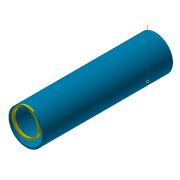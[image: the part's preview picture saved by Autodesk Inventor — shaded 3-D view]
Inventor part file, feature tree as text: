
AUTODESK INVENTOR PART (.ipt)
format: ipt  version: 2016 (Build 200138000, 138)  size: 161,792 bytes
history: native  units: in
note: dims shown in document units (in); Inventor stores cm internally (conversion verified against a paired STEP export)
features: sketch x8, extrude x4, plane x3, other x2, hole x1
ambient origin geometry x8: Origin, YZ Plane, XZ Plane, XY Plane, X Axis, Y Axis, Z Axis, Center Point
bodies: Solid1 (feature_tree)
feature tree (18):
  extrude  "Extrusion1"  Depth=0.1535in
  sketch  "Sketch2"  dims[d3=13.0709in d4=0.0in d25=0.7874in]
  plane  "Work Plane1"
  hole  "nailHole"  [1 undecoded]
  sketch  "Sketch6"  dims[d44=2.375in d45=0.2in]
  plane  "Work Plane2"
  sketch  "Sketch10"  dims[d46=0.2in d47=0.0in d48=0.1in]
  plane  "Work Plane3"
  extrude  "INSERT_GUIDE_NOTFAB"  [1 undecoded]
  extrude  "INSERT_KEY_NOTFAB"  Depth=0.2in
  other  "Work Point1"
  other  "Work Axis1"
  extrude  "shim"  Depth=0.1in
  sketch  "Sketch1"  dims[d0=3.5433in d2=0.1535in]
  sketch  "Sketch5"  dims[d27=0.1772in d28=0.75in d29=0.375in d30=0.25in d31=0.5635in d32=1.0in d33=0.8108in d43=-0.0238in]
  sketch  "Sketch11"  dims[d49=0.1in]
  sketch  "Sketch12"  dims[d50=0.5in d51=0.0in]
  sketch  "Sketch14"  dims[d52=0.5in d53=0.1181in d54=0.1969in d55=0.0in]
note: 2 required parameter values undecoded (feature->parameter linkage not recoverable at this tier; creation-order binding heuristic only, values carry confidence <= 0.55)
